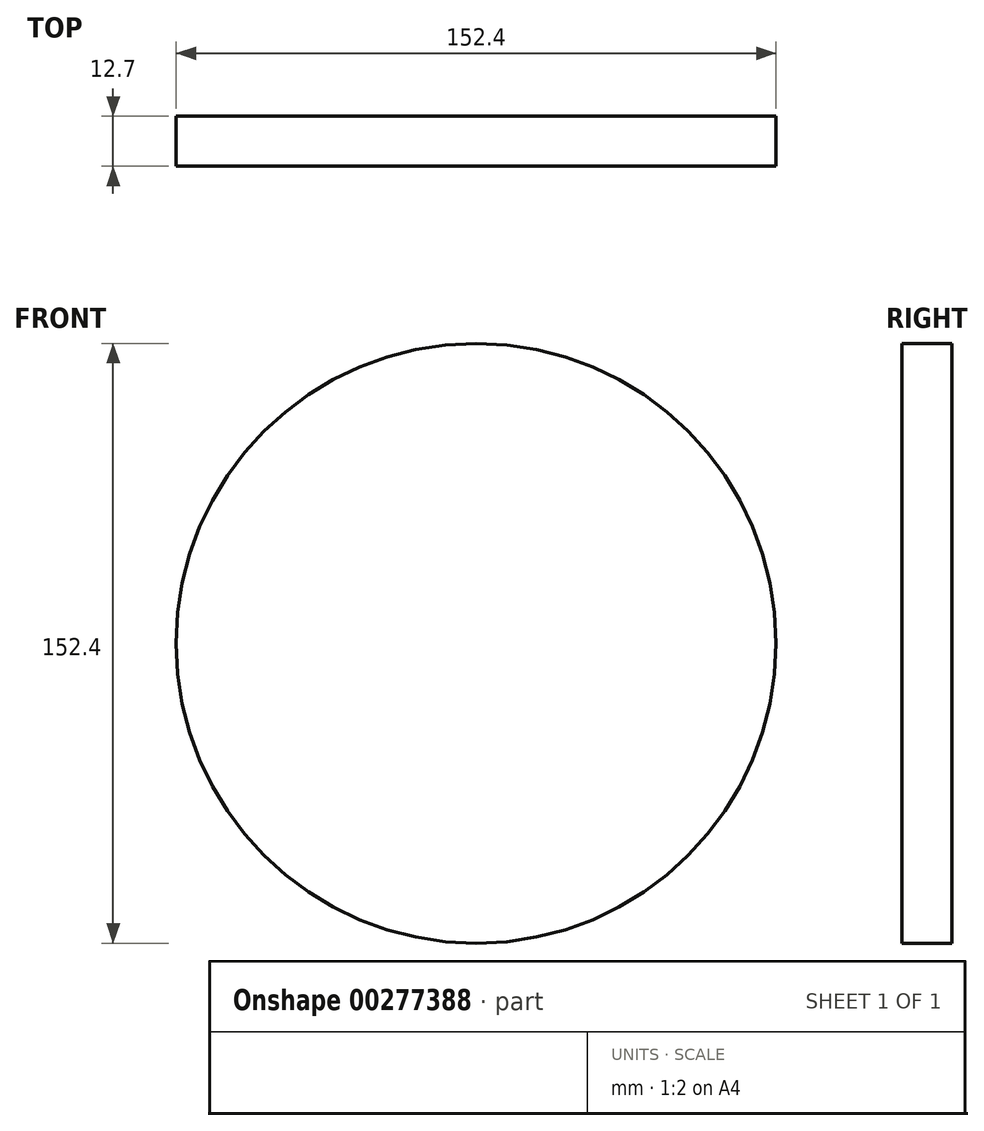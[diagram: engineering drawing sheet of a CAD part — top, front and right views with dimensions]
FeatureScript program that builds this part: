
annotation { "Feature Type Name" : "Feature", "Feature Type Description" : "" }
export const myFeature = defineFeature(function(context is Context, id is Id, definition is map)
    precondition{}
    {
        {
            var Q0;
            Q0=qCreatedBy(makeId("Front.planeOp"),FACE);
            var sketch = newSketch(context, id + "F0", { "sketchPlane" : qUnion([Q0])});
            skCircle(sketch, "E0", {"center": v(0, 0) * mm, "radius": 76.2 * mm});
            skSolve(sketch);
        }
        {
            var Q0;
            Q0=makeQuery(id+"F0.imprint","IMPRINT",FACE,{"disambiguationData":[TD([[makeQuery(id+"F0.imprint","IMPRINT",EDGE,{"derivedFrom":sQuery(id+"F0.wireOp",EDGE,"E0")}),1.0]])]});
            extrude(context, id + "F1", {"entities" : qUnion([Q0]), "depth" : 12.7 * mm});
        }
    });
